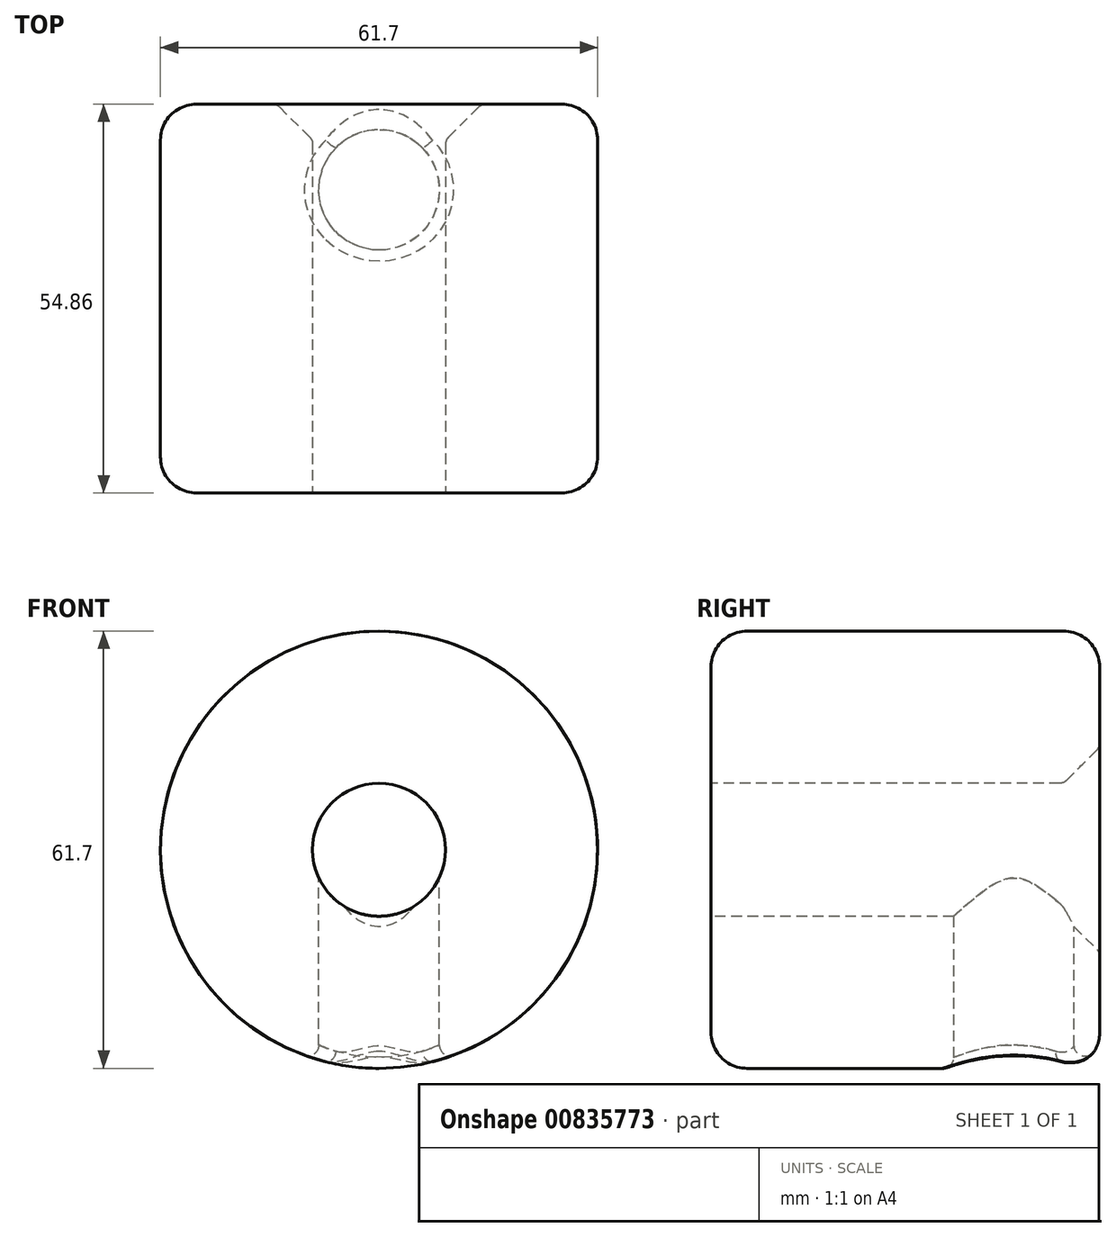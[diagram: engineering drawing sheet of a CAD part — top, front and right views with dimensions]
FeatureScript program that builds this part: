
annotation { "Feature Type Name" : "Feature", "Feature Type Description" : "" }
export const myFeature = defineFeature(function(context is Context, id is Id, definition is map)
    precondition{}
    {
        {
            var Q0;
            Q0=qCreatedBy(makeId("Front.planeOp"),FACE);
            var sketch = newSketch(context, id + "F0", { "sketchPlane" : qUnion([Q0])});
            skCircle(sketch, "E0", {"center": v(0, 0) * mm, "radius": 30.85 * mm});
            skSolve(sketch);
        }
        {
            var Q0;
            Q0=makeQuery(id+"F0.imprint","IMPRINT",FACE,{"disambiguationData":[TD([[makeQuery(id+"F0.imprint","IMPRINT",EDGE,{"derivedFrom":sQuery(id+"F0.wireOp",EDGE,"E0")}),1.0]])]});
            extrude(context, id + "F1", {"entities" : qUnion([Q0]), "depth" : 54.86 * mm, "offsetDistance" : 25.4 * mm});
        }
        {
            var Q0;
            Q0=makeQuery(id+"F1.opExtrude","CAP_EDGE",EDGE,{"disambiguationData":[OSD([sQuery(id+"F0.wireOp",EDGE,"E0")])],"isStart":false});
            var Q1;
            Q1=makeQuery(id+"F1.opExtrude","CAP_EDGE",EDGE,{"disambiguationData":[OSD([sQuery(id+"F0.wireOp",EDGE,"E0")])],"isStart":true});
            fillet(context, id + "F2", {"entities" : qUnion([Q0, Q1]), "radius" : 5.08 * mm, "tangentPropagation" : true, "allowEdgeOverflow" : false});
        }
        {
            var Q0;
            Q0=makeQuery(id+"F1.opExtrude","CAP_FACE",FACE,{"disambiguationData":[OSD([sQuery(id+"F0.wireOp",EDGE,"E0")])],"isStart":false});
            var sketch = newSketch(context, id + "F3", { "sketchPlane" : qUnion([Q0])});
            skCircle(sketch, "E1", {"center": v(0, 0) * mm, "radius": 9.39 * mm});
            skSolve(sketch);
        }
        {
            var Q0;
            Q0=makeQuery(id+"F3.imprint","IMPRINT",FACE,{"disambiguationData":[TD([[makeQuery(id+"F3.imprint","IMPRINT",EDGE,{"derivedFrom":sQuery(id+"F3.wireOp",EDGE,"E1")}),1.0]])]});
            extrude(context, id + "F4", {"entities" : qUnion([Q0]), "operationType" : NewBodyOperationType.REMOVE, "oppositeDirection" : true, "depth" : 101.6 * mm, "offsetDistance" : 25.4 * mm});
        }
        {
            var Q0;
            Q0=makeQuery(id+"F4.boolean.opBoolean","INTERSECT",EDGE,{"derivedFrom":[makeQuery(id+"F1.opExtrude","CAP_FACE",FACE,{"disambiguationData":[OSD([sQuery(id+"F0.wireOp",EDGE,"E0")])],"isStart":true}),makeQuery(id+"F4.opExtrude","SWEPT_FACE",FACE,{"disambiguationData":[OSD([sQuery(id+"F3.wireOp",EDGE,"E1")])]})]});
            chamfer(context, id + "F5", {"entities" : qUnion([Q0]), "width" : 5.08 * mm, "tangentPropagation" : true});
        }
        {
            var Q0;
            {var subQ0=makeQuery(id+"F4.opExtrude","SWEPT_FACE",FACE,{"disambiguationData":[OSD([sQuery(id+"F3.wireOp",EDGE,"E1")])]});Q0=makeQuery(id+"F5.opChamfer","BLEND_EDGE",EDGE,{"blendedFrom":[makeQuery(id+"F4.boolean.opBoolean","INTERSECT",EDGE,{"derivedFrom":[makeQuery(id+"F1.opExtrude","CAP_FACE",FACE,{"disambiguationData":[OSD([sQuery(id+"F0.wireOp",EDGE,"E0")])],"isStart":true}),subQ0]}),makeQuery(id+"F4.boolean.opBoolean","COPY",FACE,{"derivedFrom":subQ0})],"blendedInto":[makeQuery(id+"F4.boolean.opBoolean","COPY",FACE,{"derivedFrom":subQ0})]});}
            var Q1;
            {var subQ0=makeQuery(id+"F1.opExtrude","CAP_FACE",FACE,{"disambiguationData":[OSD([sQuery(id+"F0.wireOp",EDGE,"E0")])],"isStart":true});Q1=makeQuery(id+"F5.opChamfer","BLEND_EDGE",EDGE,{"blendedFrom":[makeQuery(id+"F4.boolean.opBoolean","INTERSECT",EDGE,{"derivedFrom":[subQ0,makeQuery(id+"F4.opExtrude","SWEPT_FACE",FACE,{"disambiguationData":[OSD([sQuery(id+"F3.wireOp",EDGE,"E1")])]})]}),subQ0],"blendedInto":[subQ0]});}
            fillet(context, id + "F6", {"entities" : qUnion([Q0, Q1]), "radius" : 1.27 * mm, "tangentPropagation" : true, "allowEdgeOverflow" : false});
        }
        {
            var Q0;
            Q0=qCreatedBy(makeId("Top.planeOp"),FACE);
            var sketch = newSketch(context, id + "F7", { "sketchPlane" : qUnion([Q0])});
            skCircle(sketch, "E2", {"center": v(0, -12.1) * mm, "radius": 8.5 * mm});
            skSolve(sketch);
        }
        {
            var Q0;
            Q0=makeQuery(id+"F7.imprint","IMPRINT",FACE,{"disambiguationData":[TD([[makeQuery(id+"F7.imprint","IMPRINT",EDGE,{"derivedFrom":sQuery(id+"F7.wireOp",EDGE,"E2")}),1.0]])]});
            extrude(context, id + "F8", {"entities" : qUnion([Q0]), "operationType" : NewBodyOperationType.REMOVE, "oppositeDirection" : true, "depth" : 39.37 * mm, "offsetDistance" : 25.4 * mm});
        }
        {
            var Q0;
            Q0=makeQuery(id+"F8.boolean.opBoolean","INTERSECT",EDGE,{"derivedFrom":[makeQuery(id+"F1.opExtrude","SWEPT_FACE",FACE,{"disambiguationData":[OSD([sQuery(id+"F0.wireOp",EDGE,"E0")])]}),makeQuery(id+"F8.opExtrude","SWEPT_FACE",FACE,{"disambiguationData":[OSD([sQuery(id+"F7.wireOp",EDGE,"E2")])]})]});
            var Q1;
            {var subQ0=sQuery(id+"F0.wireOp",EDGE,"E0");Q1=makeQuery(id+"F8.boolean.opBoolean","INTERSECT",EDGE,{"derivedFrom":[makeQuery(id+"F2.opFillet","BLEND_FACE",FACE,{"disambiguationData":[OSD([subQ0]),TDD([makeQuery(id+"F1.opExtrude","CAP_EDGE",EDGE,{"disambiguationData":[OSD([subQ0])],"isStart":true})])]}),makeQuery(id+"F8.opExtrude","SWEPT_FACE",FACE,{"disambiguationData":[OSD([sQuery(id+"F7.wireOp",EDGE,"E2")])]})]});}
            fillet(context, id + "F9", {"entities" : qUnion([Q0, Q1]), "radius" : 1.52 * mm, "tangentPropagation" : true, "allowEdgeOverflow" : false});
        }
    });
